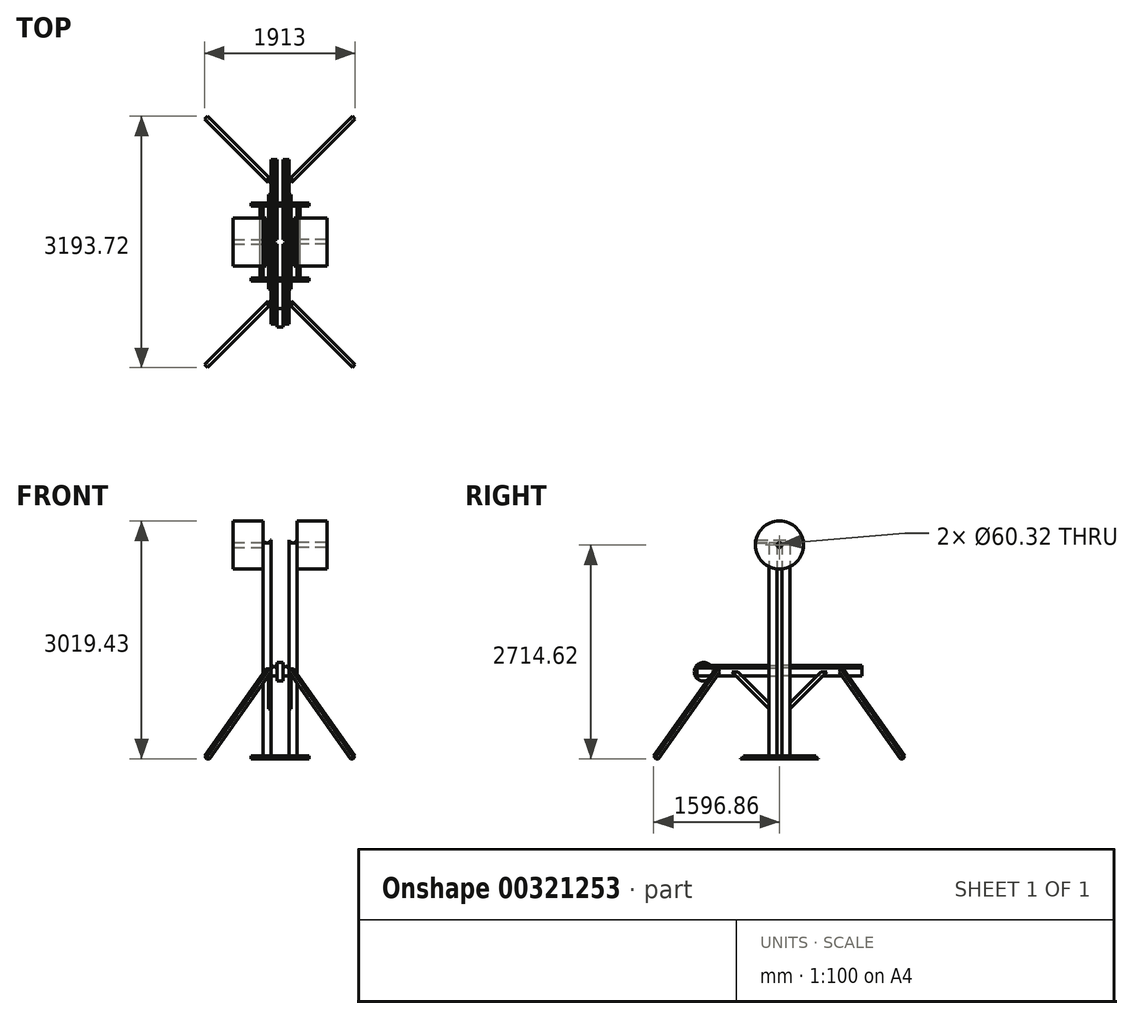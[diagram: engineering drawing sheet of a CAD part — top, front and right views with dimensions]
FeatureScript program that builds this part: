
annotation { "Feature Type Name" : "Feature", "Feature Type Description" : "" }
export const myFeature = defineFeature(function(context is Context, id is Id, definition is map)
    precondition{}
    {
        {
            var Q0;
            Q0=qCreatedBy(makeId("Top.planeOp"),FACE);
            var sketch = newSketch(context, id + "F0", { "sketchPlane" : qUnion([Q0])});
            skLineSegment(sketch, "E0.bottom", {"start": v(114.3, 30.16) * mm, "end": v(215.9, 30.16) * mm});
            skLineSegment(sketch, "E0.top", {"start": v(114.3, 131.76) * mm, "end": v(215.9, 131.76) * mm});
            skLineSegment(sketch, "E0.left", {"start": v(114.3, 30.16) * mm, "end": v(114.3, 131.76) * mm});
            skLineSegment(sketch, "E0.right", {"start": v(215.9, 30.16) * mm, "end": v(215.9, 131.76) * mm});
            skLineSegment(sketch, "E1.MirrorCS", {"start": v(-114.3, 30.16) * mm, "end": v(-215.9, 30.16) * mm});
            skLineSegment(sketch, "E2.MirrorCS", {"start": v(-114.3, 131.76) * mm, "end": v(-215.9, 131.76) * mm});
            skLineSegment(sketch, "E3.MirrorCS", {"start": v(-114.3, 30.16) * mm, "end": v(-114.3, 131.76) * mm});
            skLineSegment(sketch, "E4.MirrorCS", {"start": v(-215.9, 30.16) * mm, "end": v(-215.9, 131.76) * mm});
            skLineSegment(sketch, "E5.MirrorCS", {"start": v(-215.9, -30.16) * mm, "end": v(-215.9, -131.76) * mm});
            skLineSegment(sketch, "E6.MirrorCS", {"start": v(-114.3, -30.16) * mm, "end": v(-114.3, -131.76) * mm});
            skLineSegment(sketch, "E7.MirrorCS", {"start": v(114.3, -30.16) * mm, "end": v(215.9, -30.16) * mm});
            skLineSegment(sketch, "E8.MirrorCS", {"start": v(-114.3, -131.76) * mm, "end": v(-215.9, -131.76) * mm});
            skLineSegment(sketch, "E9.MirrorCS", {"start": v(-114.3, -30.16) * mm, "end": v(-215.9, -30.16) * mm});
            skLineSegment(sketch, "E10.MirrorCS", {"start": v(215.9, -30.16) * mm, "end": v(215.9, -131.76) * mm});
            skLineSegment(sketch, "E11.MirrorCS", {"start": v(114.3, -131.76) * mm, "end": v(215.9, -131.76) * mm});
            skLineSegment(sketch, "E12.MirrorCS", {"start": v(114.3, -30.16) * mm, "end": v(114.3, -131.76) * mm});
            skSolve(sketch);
        }
        {
            var Q0;
            Q0=makeQuery(id+"F0.imprint","IMPRINT",FACE,{"disambiguationData":[TD([[makeQuery(id+"F0.imprint","IMPRINT",EDGE,{"derivedFrom":sQuery(id+"F0.wireOp",EDGE,"E5.MirrorCS")}),1.0]])]});
            var Q1;
            Q1=makeQuery(id+"F0.imprint","IMPRINT",FACE,{"disambiguationData":[TD([[makeQuery(id+"F0.imprint","IMPRINT",EDGE,{"derivedFrom":sQuery(id+"F0.wireOp",EDGE,"E1.MirrorCS")}),-1.0]])]});
            var Q2;
            Q2=makeQuery(id+"F0.imprint","IMPRINT",FACE,{"disambiguationData":[TD([[makeQuery(id+"F0.imprint","IMPRINT",EDGE,{"derivedFrom":sQuery(id+"F0.wireOp",EDGE,"E0.bottom")}),1.0]])]});
            var Q3;
            Q3=makeQuery(id+"F0.imprint","IMPRINT",FACE,{"disambiguationData":[TD([[makeQuery(id+"F0.imprint","IMPRINT",EDGE,{"derivedFrom":sQuery(id+"F0.wireOp",EDGE,"E7.MirrorCS")}),-1.0]])]});
            extrude(context, id + "F1", {"entities" : qUnion([Q0, Q1, Q2, Q3]), "depth" : 2743.2 * mm});
        }
        {
            var Q0;
            Q0=makeQuery(id+"F1.opExtrude","SWEPT_FACE",FACE,{"disambiguationData":[OSD([sQuery(id+"F0.wireOp",EDGE,"E0.bottom")])]});
            var sketch = newSketch(context, id + "F2", { "sketchPlane" : qUnion([Q0])});
            skLineSegment(sketch, "E13.bottom", {"start": v(114.3, 1155.7) * mm, "end": v(38.1, 1155.7) * mm});
            skLineSegment(sketch, "E13.top", {"start": v(114.3, 1054.1) * mm, "end": v(38.1, 1054.1) * mm});
            skLineSegment(sketch, "E13.left", {"start": v(114.3, 1155.7) * mm, "end": v(114.3, 1054.1) * mm});
            skLineSegment(sketch, "E13.right", {"start": v(38.1, 1155.7) * mm, "end": v(38.1, 1054.1) * mm});
            skLineSegment(sketch, "E14", {"start": v(0, 1227.15) * mm, "end": v(0, 1056.68) * mm, "construction": true});
            skLineSegment(sketch, "E15.MirrorCS", {"start": v(-114.3, 1155.7) * mm, "end": v(-38.1, 1155.7) * mm});
            skLineSegment(sketch, "E16.MirrorCS", {"start": v(-114.3, 1054.1) * mm, "end": v(-38.1, 1054.1) * mm});
            skLineSegment(sketch, "E17.MirrorCS", {"start": v(-114.3, 1155.7) * mm, "end": v(-114.3, 1054.1) * mm});
            skLineSegment(sketch, "E18.MirrorCS", {"start": v(-38.1, 1155.7) * mm, "end": v(-38.1, 1054.1) * mm});
            skLineSegment(sketch, "E19", {"start": v(47.72, 1155.7) * mm, "end": v(74.66, 1182.64) * mm});
            skLineSegment(sketch, "E20", {"start": v(74.66, 1182.64) * mm, "end": v(101.6, 1155.7) * mm});
            skLineSegment(sketch, "E21.MirrorCS", {"start": v(-47.72, 1155.7) * mm, "end": v(-74.66, 1182.64) * mm});
            skLineSegment(sketch, "E22.MirrorCS", {"start": v(-74.66, 1182.64) * mm, "end": v(-101.6, 1155.7) * mm});
            skSolve(sketch);
        }
        {
            var Q0;
            Q0=makeQuery(id+"F2.imprint","IMPRINT",FACE,{"disambiguationData":[TD([[makeQuery(id+"F2.imprint","IMPRINT",EDGE,{"derivedFrom":sQuery(id+"F2.wireOp",EDGE,"E15.MirrorCS")}),-1.0]])]});
            var Q1;
            Q1=makeQuery(id+"F2.imprint","IMPRINT",FACE,{"disambiguationData":[TD([[makeQuery(id+"F2.imprint","IMPRINT",EDGE,{"derivedFrom":sQuery(id+"F2.wireOp",EDGE,"E13.bottom")}),1.0]])]});
            var Q2;
            {var subQ0=sQuery(id+"F2.wireOp",EDGE,"E21.MirrorCS");Q2=makeQuery(id+"F2.imprint","IMPRINT",FACE,{"disambiguationData":[TD([[makeQuery(id+"F2.imprint","IMPRINT",EDGE,{"derivedFrom":subQ0}),1.0]])]});}
            var Q3;
            {var subQ0=sQuery(id+"F2.wireOp",EDGE,"E19");Q3=makeQuery(id+"F2.imprint","IMPRINT",FACE,{"disambiguationData":[TD([[makeQuery(id+"F2.imprint","IMPRINT",EDGE,{"derivedFrom":subQ0}),-1.0]])]});}
            extrude(context, id + "F3", {"entities" : qUnion([Q0, Q1, Q2, Q3]), "oppositeDirection" : true, "depth" : 1016 * mm});
        }
        {
            var Q0;
            Q0=makeQuery(id+"F3.opExtrude","SWEPT_BODY",BODY,{"disambiguationData":[OSD([sQuery(id+"F2.wireOp",EDGE,"E13.bottom"),sQuery(id+"F2.wireOp",EDGE,"E13.top"),sQuery(id+"F2.wireOp",EDGE,"E13.left"),sQuery(id+"F2.wireOp",EDGE,"E13.right"),sQuery(id+"F2.wireOp",EDGE,"E19"),sQuery(id+"F2.wireOp",EDGE,"E20")])]});
            var Q1;
            Q1=makeQuery(id+"F3.opExtrude","SWEPT_BODY",BODY,{"disambiguationData":[OSD([sQuery(id+"F2.wireOp",EDGE,"E15.MirrorCS"),sQuery(id+"F2.wireOp",EDGE,"E16.MirrorCS"),sQuery(id+"F2.wireOp",EDGE,"E17.MirrorCS"),sQuery(id+"F2.wireOp",EDGE,"E18.MirrorCS"),sQuery(id+"F2.wireOp",EDGE,"E21.MirrorCS"),sQuery(id+"F2.wireOp",EDGE,"E22.MirrorCS")])]});
            var Q2;
            Q2=qCreatedBy(makeId("Front.planeOp"),FACE);
            mirror(context, id + "F4", {"entities" : qUnion([Q0, Q1]), "mirrorPlane" : qUnion([Q2])});
        }
        {
            var Q0;
            Q0=makeQuery(id+"F4.opPattern","COPY",FACE,{"derivedFrom":makeQuery(id+"F3.opExtrude","SWEPT_FACE",FACE,{"disambiguationData":[OSD([sQuery(id+"F2.wireOp",EDGE,"E18.MirrorCS")])]}),"instanceName":"1"});
            var sketch = newSketch(context, id + "F5", { "sketchPlane" : qUnion([Q0])});
            skCircle(sketch, "E23", {"center": v(-965.2, 1104.9) * mm, "radius": 117.48 * mm});
            skSolve(sketch);
        }
        {
            var Q0;
            {var subQ1=sQuery(id+"F2.wireOp",EDGE,"E18.MirrorCS");var subQ6=makeQuery(id+"F4.opPattern","COPY",EDGE,{"derivedFrom":makeQuery(id+"F3.opExtrude","CAP_EDGE",EDGE,{"disambiguationData":[OSD([subQ1])],"isStart":false}),"instanceName":"1"});Q0=makeQuery(id+"F5.imprint","IMPRINT",FACE,{"disambiguationData":[TD([[makeQuery(id+"F5.imprint","IMPRINT",EDGE,{"derivedFrom":subQ6}),-1.0]])]});}
            var Q1;
            {var subQ1=sQuery(id+"F2.wireOp",EDGE,"E18.MirrorCS");var subQ6=makeQuery(id+"F4.opPattern","COPY",EDGE,{"derivedFrom":makeQuery(id+"F3.opExtrude","CAP_EDGE",EDGE,{"disambiguationData":[OSD([subQ1])],"isStart":false}),"instanceName":"1"});Q1=makeQuery(id+"F5.imprint","IMPRINT",FACE,{"disambiguationData":[TD([[makeQuery(id+"F5.imprint","IMPRINT",EDGE,{"derivedFrom":subQ6}),1.0]])]});}
            extrude(context, id + "F6", {"entities" : qUnion([Q0, Q1]), "depth" : 76.2 * mm});
        }
        {
            var Q0;
            Q0=makeQuery(id+"F4.opPattern","COPY",FACE,{"derivedFrom":makeQuery(id+"F3.opExtrude","SWEPT_FACE",FACE,{"disambiguationData":[OSD([sQuery(id+"F2.wireOp",EDGE,"E13.left")])]}),"instanceName":"1"});
            var sketch = newSketch(context, id + "F7", { "sketchPlane" : qUnion([Q0])});
            skLineSegment(sketch, "E24.0", {"start": v(-131.76, 2743.2) * mm, "end": v(-131.76, 0) * mm, "construction": true});
            skLineSegment(sketch, "E25", {"start": v(-564.5, 1104.9) * mm, "end": v(-486.45, 1104.9) * mm, "construction": true});
            skLineSegment(sketch, "E26", {"start": v(-564.5, 1104.9) * mm, "end": v(-564.5, 1155.7) * mm, "construction": true});
            skLineSegment(sketch, "E27", {"start": v(-564.5, 1104.9) * mm, "end": v(-564.5, 1054.1) * mm, "construction": true});
            skLineSegment(sketch, "E28", {"start": v(-131.76, 635) * mm, "end": v(-601.66, 1104.9) * mm});
            skLineSegment(sketch, "E29", {"start": v(-601.66, 1104.9) * mm, "end": v(-525.47, 1104.9) * mm});
            skLineSegment(sketch, "E30", {"start": v(-525.47, 1104.9) * mm, "end": v(-131.76, 711.19) * mm});
            skLineSegment(sketch, "E31", {"start": v(-131.76, 711.19) * mm, "end": v(-131.76, 635) * mm});
            skSolve(sketch);
        }
        {
            var Q0;
            {var subQ0=sQuery(id+"F7.wireOp",EDGE,"E31");Q0=makeQuery(id+"F7.imprint","IMPRINT",FACE,{"disambiguationData":[TD([[makeQuery(id+"F7.imprint","IMPRINT",EDGE,{"derivedFrom":subQ0}),-1.0]])]});}
            var Q1;
            {var subQ0=sQuery(id+"F7.wireOp",EDGE,"E29");Q1=makeQuery(id+"F7.imprint","IMPRINT",FACE,{"disambiguationData":[TD([[makeQuery(id+"F7.imprint","IMPRINT",EDGE,{"derivedFrom":subQ0}),-1.0]])]});}
            extrude(context, id + "F8", {"entities" : qUnion([Q0, Q1]), "depth" : 26.92 * mm});
        }
        {
            var Q0;
            Q0=makeQuery(id+"FNKVfird8vsgjME_14.opPattern","COPY",BODY,{"derivedFrom":makeQuery(id+"F8.opExtrude","SWEPT_BODY",BODY,{"disambiguationData":[OSD([sQuery(id+"F7.wireOp",EDGE,"E28"),sQuery(id+"F7.wireOp",EDGE,"E29"),sQuery(id+"F7.wireOp",EDGE,"E30"),sQuery(id+"F7.wireOp",EDGE,"E31")])]}),"instanceName":"1"});
            var Q1;
            Q1=makeQuery(id+"F8.opExtrude","SWEPT_BODY",BODY,{"disambiguationData":[OSD([sQuery(id+"F7.wireOp",EDGE,"E28"),sQuery(id+"F7.wireOp",EDGE,"E29"),sQuery(id+"F7.wireOp",EDGE,"E30"),sQuery(id+"F7.wireOp",EDGE,"E31")])]});
            var Q2;
            Q2=qCreatedBy(makeId("Front.planeOp"),FACE);
            mirror(context, id + "F9", {"entities" : qUnion([Q0, Q1]), "mirrorPlane" : qUnion([Q2])});
        }
        {
            var Q0;
            Q0=makeQuery(id+"F8.opExtrude","SWEPT_BODY",BODY,{"disambiguationData":[OSD([sQuery(id+"F7.wireOp",EDGE,"E28"),sQuery(id+"F7.wireOp",EDGE,"E29"),sQuery(id+"F7.wireOp",EDGE,"E30"),sQuery(id+"F7.wireOp",EDGE,"E31")])]});
            var Q1;
            Q1=makeQuery(id+"FNKVfird8vsgjME_14.opPattern","COPY",BODY,{"derivedFrom":makeQuery(id+"F8.opExtrude","SWEPT_BODY",BODY,{"disambiguationData":[OSD([sQuery(id+"F7.wireOp",EDGE,"E28"),sQuery(id+"F7.wireOp",EDGE,"E29"),sQuery(id+"F7.wireOp",EDGE,"E30"),sQuery(id+"F7.wireOp",EDGE,"E31")])]}),"instanceName":"1"});
            var Q2;
            Q2=makeQuery(id+"F9.opPattern","COPY",BODY,{"derivedFrom":makeQuery(id+"FNKVfird8vsgjME_14.opPattern","COPY",BODY,{"derivedFrom":makeQuery(id+"F8.opExtrude","SWEPT_BODY",BODY,{"disambiguationData":[OSD([sQuery(id+"F7.wireOp",EDGE,"E28"),sQuery(id+"F7.wireOp",EDGE,"E29"),sQuery(id+"F7.wireOp",EDGE,"E30"),sQuery(id+"F7.wireOp",EDGE,"E31")])]}),"instanceName":"1"}),"instanceName":"1"});
            var Q3;
            Q3=makeQuery(id+"F9.opPattern","COPY",BODY,{"derivedFrom":makeQuery(id+"F8.opExtrude","SWEPT_BODY",BODY,{"disambiguationData":[OSD([sQuery(id+"F7.wireOp",EDGE,"E28"),sQuery(id+"F7.wireOp",EDGE,"E29"),sQuery(id+"F7.wireOp",EDGE,"E30"),sQuery(id+"F7.wireOp",EDGE,"E31")])]}),"instanceName":"1"});
            var Q4;
            Q4=qCreatedBy(makeId("Right.planeOp"),FACE);
            mirror(context, id + "F10", {"entities" : qUnion([Q0, Q1, Q2, Q3]), "mirrorPlane" : qUnion([Q4])});
        }
        {
            var Q0;
            Q0=qCreatedBy(makeId("Front.planeOp"),FACE);
            var sketch = newSketch(context, id + "F11", { "sketchPlane" : qUnion([Q0])});
            skLineSegment(sketch, "E32.0", {"start": v(114.3, 2743.2) * mm, "end": v(114.3, 0) * mm, "construction": true});
            skLineSegment(sketch, "E32.1", {"start": v(-114.3, 2743.2) * mm, "end": v(-114.3, 0) * mm, "construction": true});
            skLineSegment(sketch, "E32.2", {"start": v(-215.9, 2743.2) * mm, "end": v(-215.9, 0) * mm, "construction": true});
            skLineSegment(sketch, "E32.3", {"start": v(215.9, 2743.2) * mm, "end": v(215.9, 0) * mm, "construction": true});
            skLineSegment(sketch, "E33", {"start": v(-114.3, 0) * mm, "end": v(-114.3, 38.1) * mm});
            skLineSegment(sketch, "E34", {"start": v(-114.3, 38.1) * mm, "end": v(-111.12, 38.1) * mm});
            skLineSegment(sketch, "E35", {"start": v(-111.12, 38.1) * mm, "end": v(-111.12, 3.18) * mm});
            skLineSegment(sketch, "E36", {"start": v(-111.12, 3.18) * mm, "end": v(-76.2, 3.18) * mm});
            skLineSegment(sketch, "E37", {"start": v(-76.2, 3.18) * mm, "end": v(-76.2, 0) * mm});
            skLineSegment(sketch, "E38", {"start": v(-76.2, 0) * mm, "end": v(-114.3, 0) * mm});
            skLineSegment(sketch, "E39", {"start": v(-215.9, 0) * mm, "end": v(-215.9, 38.1) * mm});
            skLineSegment(sketch, "E40", {"start": v(-215.9, 38.1) * mm, "end": v(-219.07, 38.1) * mm});
            skLineSegment(sketch, "E41", {"start": v(-219.07, 38.1) * mm, "end": v(-219.07, 3.17) * mm});
            skLineSegment(sketch, "E42", {"start": v(-219.07, 3.17) * mm, "end": v(-254, 3.17) * mm});
            skLineSegment(sketch, "E43", {"start": v(-254, 3.17) * mm, "end": v(-254, 0) * mm});
            skLineSegment(sketch, "E44", {"start": v(-254, 0) * mm, "end": v(-215.9, 0) * mm});
            skLineSegment(sketch, "E45.MirrorCS", {"start": v(114.3, 0) * mm, "end": v(114.3, 38.1) * mm});
            skLineSegment(sketch, "E46.MirrorCS", {"start": v(111.12, 38.1) * mm, "end": v(111.12, 3.18) * mm});
            skLineSegment(sketch, "E47.MirrorCS", {"start": v(76.2, 0) * mm, "end": v(114.3, 0) * mm});
            skLineSegment(sketch, "E48.MirrorCS", {"start": v(111.12, 3.18) * mm, "end": v(76.2, 3.18) * mm});
            skLineSegment(sketch, "E49.MirrorCS", {"start": v(76.2, 3.18) * mm, "end": v(76.2, 0) * mm});
            skLineSegment(sketch, "E50.MirrorCS", {"start": v(114.3, 38.1) * mm, "end": v(111.12, 38.1) * mm});
            skLineSegment(sketch, "E51.MirrorCS", {"start": v(254, 3.17) * mm, "end": v(254, 0) * mm});
            skLineSegment(sketch, "E52.MirrorCS", {"start": v(215.9, 38.1) * mm, "end": v(219.07, 38.1) * mm});
            skLineSegment(sketch, "E53.MirrorCS", {"start": v(215.9, 0) * mm, "end": v(215.9, 38.1) * mm});
            skLineSegment(sketch, "E54.MirrorCS", {"start": v(219.07, 3.17) * mm, "end": v(254, 3.17) * mm});
            skLineSegment(sketch, "E55.MirrorCS", {"start": v(254, 0) * mm, "end": v(215.9, 0) * mm});
            skLineSegment(sketch, "E56.MirrorCS", {"start": v(219.07, 38.1) * mm, "end": v(219.07, 3.17) * mm});
            skSolve(sketch);
        }
        {
            var Q0;
            Q0=makeQuery(id+"F11.imprint","IMPRINT",FACE,{"disambiguationData":[TD([[makeQuery(id+"F11.imprint","IMPRINT",EDGE,{"derivedFrom":sQuery(id+"F11.wireOp",EDGE,"E39")}),1.0]])]});
            var Q1;
            Q1=makeQuery(id+"F11.imprint","IMPRINT",FACE,{"disambiguationData":[TD([[makeQuery(id+"F11.imprint","IMPRINT",EDGE,{"derivedFrom":sQuery(id+"F11.wireOp",EDGE,"E33")}),-1.0]])]});
            var Q2;
            Q2=makeQuery(id+"F11.imprint","IMPRINT",FACE,{"disambiguationData":[TD([[makeQuery(id+"F11.imprint","IMPRINT",EDGE,{"derivedFrom":sQuery(id+"F11.wireOp",EDGE,"E49.MirrorCS")}),1.0]])]});
            var Q3;
            Q3=makeQuery(id+"F11.imprint","IMPRINT",FACE,{"disambiguationData":[TD([[makeQuery(id+"F11.imprint","IMPRINT",EDGE,{"derivedFrom":sQuery(id+"F11.wireOp",EDGE,"E51.MirrorCS")}),-1.0]])]});
            extrude(context, id + "F12", {"entities" : qUnion([Q0, Q1, Q2, Q3]), "endBound" : BoundingType.SYMMETRIC, "depth" : 914.4 * mm});
        }
        {
            var Q0;
            Q0=qCreatedBy(makeId("Right.planeOp"),FACE);
            var sketch = newSketch(context, id + "F13", { "sketchPlane" : qUnion([Q0])});
            skLineSegment(sketch, "E57.0", {"start": v(-457.2, 0) * mm, "end": v(-457.2, 38.1) * mm});
            skLineSegment(sketch, "E58", {"start": v(-457.2, 38.1) * mm, "end": v(-460.38, 38.1) * mm});
            skLineSegment(sketch, "E59", {"start": v(-460.38, 38.1) * mm, "end": v(-460.38, 3.18) * mm});
            skLineSegment(sketch, "E60", {"start": v(-460.38, 3.18) * mm, "end": v(-495.3, 3.17) * mm});
            skLineSegment(sketch, "E61", {"start": v(-495.3, 3.17) * mm, "end": v(-495.3, 0) * mm});
            skLineSegment(sketch, "E62", {"start": v(-495.3, 0) * mm, "end": v(-457.2, 0) * mm});
            skLineSegment(sketch, "E63.MirrorCS", {"start": v(495.3, 3.17) * mm, "end": v(495.3, 0) * mm});
            skLineSegment(sketch, "E64.MirrorCS", {"start": v(457.2, 38.1) * mm, "end": v(460.38, 38.1) * mm});
            skLineSegment(sketch, "E65.MirrorCS", {"start": v(460.38, 3.18) * mm, "end": v(495.3, 3.17) * mm});
            skLineSegment(sketch, "E66.MirrorCS", {"start": v(460.38, 38.1) * mm, "end": v(460.38, 3.18) * mm});
            skLineSegment(sketch, "E67.MirrorCS", {"start": v(457.2, 0) * mm, "end": v(457.2, 38.1) * mm});
            skLineSegment(sketch, "E68.MirrorCS", {"start": v(495.3, 0) * mm, "end": v(457.2, 0) * mm});
            skSolve(sketch);
        }
        {
            var Q0;
            Q0=makeQuery(id+"F13.imprint","IMPRINT",FACE,{"disambiguationData":[TD([[makeQuery(id+"F13.imprint","IMPRINT",EDGE,{"derivedFrom":sQuery(id+"F13.wireOp",EDGE,"E57.0")}),1.0]])]});
            var Q1;
            Q1=makeQuery(id+"F13.imprint","IMPRINT",FACE,{"disambiguationData":[TD([[makeQuery(id+"F13.imprint","IMPRINT",EDGE,{"derivedFrom":sQuery(id+"F13.wireOp",EDGE,"E63.MirrorCS")}),-1.0]])]});
            extrude(context, id + "F14", {"entities" : qUnion([Q0, Q1]), "endBound" : BoundingType.SYMMETRIC, "depth" : 736.6 * mm});
        }
        {
            var Q0;
            Q0=makeQuery(id+"F1.opExtrude","SWEPT_FACE",FACE,{"disambiguationData":[OSD([sQuery(id+"F0.wireOp",EDGE,"E0.right")])]});
            var sketch = newSketch(context, id + "F15", { "sketchPlane" : qUnion([Q0])});
            skCircle(sketch, "E69", {"center": v(0, 2714.63) * mm, "radius": 30.16 * mm});
            skCircle(sketch, "E70", {"center": v(0, 2714.63) * mm, "radius": 304.8 * mm});
            skSolve(sketch);
        }
        {
            var Q0;
            Q0=qCreatedBy(makeId("Front.planeOp"),FACE);
            var sketch = newSketch(context, id + "F16", { "sketchPlane" : qUnion([Q0])});
            skLineSegment(sketch, "E71.0", {"start": v(-114.3, 2743.2) * mm, "end": v(-215.9, 2743.2) * mm, "construction": true});
            skLineSegment(sketch, "E72.0", {"start": v(114.3, 2743.2) * mm, "end": v(215.9, 2743.2) * mm, "construction": true});
            skLineSegment(sketch, "E73", {"start": v(-215.9, 2743.2) * mm, "end": v(-215.9, 2781.3) * mm});
            skLineSegment(sketch, "E74", {"start": v(-215.9, 2781.3) * mm, "end": v(-212.72, 2781.3) * mm});
            skLineSegment(sketch, "E75", {"start": v(-212.72, 2781.3) * mm, "end": v(-212.72, 2746.38) * mm});
            skLineSegment(sketch, "E76", {"start": v(-212.72, 2746.38) * mm, "end": v(-177.8, 2746.38) * mm});
            skLineSegment(sketch, "E77", {"start": v(-177.8, 2746.38) * mm, "end": v(-177.8, 2743.2) * mm});
            skLineSegment(sketch, "E78", {"start": v(-177.8, 2743.2) * mm, "end": v(-215.9, 2743.2) * mm});
            skLineSegment(sketch, "E79", {"start": v(-114.3, 2743.2) * mm, "end": v(-152.4, 2743.2) * mm});
            skLineSegment(sketch, "E80", {"start": v(-152.4, 2743.2) * mm, "end": v(-152.4, 2746.38) * mm});
            skLineSegment(sketch, "E81", {"start": v(-152.4, 2746.38) * mm, "end": v(-117.47, 2746.38) * mm});
            skLineSegment(sketch, "E82", {"start": v(-117.47, 2746.38) * mm, "end": v(-117.47, 2781.3) * mm});
            skLineSegment(sketch, "E83", {"start": v(-117.47, 2781.3) * mm, "end": v(-114.3, 2781.3) * mm});
            skLineSegment(sketch, "E84", {"start": v(-114.3, 2781.3) * mm, "end": v(-114.3, 2743.2) * mm});
            skLineSegment(sketch, "E85.MirrorCS", {"start": v(152.4, 2743.2) * mm, "end": v(152.4, 2746.38) * mm});
            skLineSegment(sketch, "E86.MirrorCS", {"start": v(117.47, 2781.3) * mm, "end": v(114.3, 2781.3) * mm});
            skLineSegment(sketch, "E87.MirrorCS", {"start": v(177.8, 2746.38) * mm, "end": v(177.8, 2743.2) * mm});
            skLineSegment(sketch, "E88.MirrorCS", {"start": v(114.3, 2781.3) * mm, "end": v(114.3, 2743.2) * mm});
            skLineSegment(sketch, "E89.MirrorCS", {"start": v(117.47, 2746.38) * mm, "end": v(117.47, 2781.3) * mm});
            skLineSegment(sketch, "E90.MirrorCS", {"start": v(152.4, 2746.38) * mm, "end": v(117.47, 2746.38) * mm});
            skLineSegment(sketch, "E91.MirrorCS", {"start": v(114.3, 2743.2) * mm, "end": v(152.4, 2743.2) * mm});
            skLineSegment(sketch, "E92.MirrorCS", {"start": v(215.9, 2781.3) * mm, "end": v(212.72, 2781.3) * mm});
            skLineSegment(sketch, "E93.MirrorCS", {"start": v(215.9, 2743.2) * mm, "end": v(215.9, 2781.3) * mm});
            skLineSegment(sketch, "E94.MirrorCS", {"start": v(212.72, 2781.3) * mm, "end": v(212.72, 2746.38) * mm});
            skLineSegment(sketch, "E95.MirrorCS", {"start": v(212.72, 2746.38) * mm, "end": v(177.8, 2746.38) * mm});
            skLineSegment(sketch, "E96.MirrorCS", {"start": v(177.8, 2743.2) * mm, "end": v(215.9, 2743.2) * mm});
            skSolve(sketch);
        }
        {
            var Q0;
            Q0=makeQuery(id+"F16.imprint","IMPRINT",FACE,{"disambiguationData":[TD([[makeQuery(id+"F16.imprint","IMPRINT",EDGE,{"derivedFrom":sQuery(id+"F16.wireOp",EDGE,"E85.MirrorCS")}),1.0]])]});
            var Q1;
            Q1=makeQuery(id+"F16.imprint","IMPRINT",FACE,{"disambiguationData":[TD([[makeQuery(id+"F16.imprint","IMPRINT",EDGE,{"derivedFrom":sQuery(id+"F16.wireOp",EDGE,"E92.MirrorCS")}),1.0]])]});
            var Q2;
            Q2=makeQuery(id+"F16.imprint","IMPRINT",FACE,{"disambiguationData":[TD([[makeQuery(id+"F16.imprint","IMPRINT",EDGE,{"derivedFrom":sQuery(id+"F16.wireOp",EDGE,"E73")}),-1.0]])]});
            var Q3;
            Q3=makeQuery(id+"F16.imprint","IMPRINT",FACE,{"disambiguationData":[TD([[makeQuery(id+"F16.imprint","IMPRINT",EDGE,{"derivedFrom":sQuery(id+"F16.wireOp",EDGE,"E79")}),-1.0]])]});
            extrude(context, id + "F17", {"entities" : qUnion([Q0, Q1, Q2, Q3]), "endBound" : BoundingType.SYMMETRIC, "depth" : 609.6 * mm});
        }
        {
            var Q0;
            {var subQ0=sQuery(id+"F0.wireOp",EDGE,"E0.right");var subQ5=makeQuery(id+"F1.opExtrude","CAP_EDGE",EDGE,{"disambiguationData":[OSD([subQ0])],"isStart":false});Q0=makeQuery(id+"F15.imprint","IMPRINT",FACE,{"disambiguationData":[TD([[makeQuery(id+"F15.imprint","IMPRINT",EDGE,{"derivedFrom":subQ5}),-1.0]])]});}
            var Q1;
            {var subQ0=sQuery(id+"F0.wireOp",EDGE,"E0.right");var subQ5=makeQuery(id+"F1.opExtrude","CAP_EDGE",EDGE,{"disambiguationData":[OSD([subQ0])],"isStart":false});Q1=makeQuery(id+"F15.imprint","IMPRINT",FACE,{"disambiguationData":[TD([[makeQuery(id+"F15.imprint","IMPRINT",EDGE,{"derivedFrom":subQ5}),1.0]])]});}
            extrude(context, id + "F18", {"entities" : qUnion([Q0, Q1]), "depth" : 381 * mm});
        }
        {
            var Q0;
            Q0=makeQuery(id+"F18.opExtrude","SWEPT_BODY",BODY,{"disambiguationData":[OSD([sQuery(id+"F15.wireOp",EDGE,"E70")])]});
            var Q1;
            Q1=qCreatedBy(makeId("Right.planeOp"),FACE);
            mirror(context, id + "F19", {"entities" : qUnion([Q0]), "mirrorPlane" : qUnion([Q1])});
        }
        {
            var Q0;
            Q0=makeQuery(id+"F12.opExtrude","CAP_EDGE",EDGE,{"disambiguationData":[OSD([sQuery(id+"F11.wireOp",EDGE,"E56.MirrorCS")])],"isStart":false});
            cPlane(context, id + "F20", {"entities" : qUnion([Q0]), "cplaneType" : CPlaneType.LINE_ANGLE, "offset" : 25.4 * mm, "angle" : 45 * degree, "width" : 152.4 * mm, "height" : 152.4 * mm});
        }
        {
            var Q0;
            Q0=qCreatedBy(id+"F20.planeOp",FACE);
            var sketch = newSketch(context, id + "F21", { "sketchPlane" : qUnion([Q0])});
            skLineSegment(sketch, "E97.0", {"start": v(820.57, 1054.1) * mm, "end": v(102.15, 1054.1) * mm, "construction": true});
            skLineSegment(sketch, "E98.0", {"start": v(502.9, 0) * mm, "end": v(-143.68, 0) * mm, "construction": true});
            skLineSegment(sketch, "E99", {"start": v(502.9, 0) * mm, "end": v(2416.7, 0) * mm, "construction": true});
            skLineSegment(sketch, "E100", {"start": v(639.28, 1104.9) * mm, "end": v(1744.18, 0) * mm});
            skLineSegment(sketch, "E101", {"start": v(639.28, 1104.9) * mm, "end": v(675.2, 1140.82) * mm});
            skLineSegment(sketch, "E102", {"start": v(675.2, 1140.82) * mm, "end": v(1780.1, 35.92) * mm});
            skLineSegment(sketch, "E103", {"start": v(1744.18, 0) * mm, "end": v(1780.1, 35.92) * mm});
            skSolve(sketch);
        }
        {
            var Q0;
            Q0=makeQuery(id+"F21.imprint","IMPRINT",FACE,{"disambiguationData":[TD([[makeQuery(id+"F21.imprint","IMPRINT",EDGE,{"derivedFrom":sQuery(id+"F21.wireOp",EDGE,"E100")}),1.0]])]});
            extrude(context, id + "F22", {"entities" : qUnion([Q0]), "depth" : 50.8 * mm});
        }
        {
            var Q0;
            Q0=makeQuery(id+"F22.opExtrude","SWEPT_BODY",BODY,{"disambiguationData":[OSD([sQuery(id+"F21.wireOp",EDGE,"E100"),sQuery(id+"F21.wireOp",EDGE,"E101"),sQuery(id+"F21.wireOp",EDGE,"E102"),sQuery(id+"F21.wireOp",EDGE,"E103")])]});
            var Q1;
            Q1=qCreatedBy(makeId("Right.planeOp"),FACE);
            mirror(context, id + "F23", {"entities" : qUnion([Q0]), "mirrorPlane" : qUnion([Q1])});
        }
        {
            var Q0;
            Q0=makeQuery(id+"F22.opExtrude","SWEPT_BODY",BODY,{"disambiguationData":[OSD([sQuery(id+"F21.wireOp",EDGE,"E100"),sQuery(id+"F21.wireOp",EDGE,"E101"),sQuery(id+"F21.wireOp",EDGE,"E102"),sQuery(id+"F21.wireOp",EDGE,"E103")])]});
            var Q1;
            Q1=makeQuery(id+"F23.opPattern","COPY",BODY,{"derivedFrom":makeQuery(id+"F22.opExtrude","SWEPT_BODY",BODY,{"disambiguationData":[OSD([sQuery(id+"F21.wireOp",EDGE,"E100"),sQuery(id+"F21.wireOp",EDGE,"E101"),sQuery(id+"F21.wireOp",EDGE,"E102"),sQuery(id+"F21.wireOp",EDGE,"E103")])]}),"instanceName":"1"});
            var Q2;
            Q2=qCreatedBy(makeId("Front.planeOp"),FACE);
            mirror(context, id + "F24", {"entities" : qUnion([Q0, Q1]), "mirrorPlane" : qUnion([Q2])});
        }
    });
